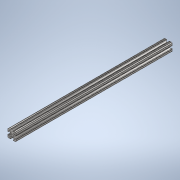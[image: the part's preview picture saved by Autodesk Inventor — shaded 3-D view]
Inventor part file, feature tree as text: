
AUTODESK INVENTOR PART (.ipt)
format: ipt  version: 2020 (Build 240168000, 168)  size: 241,152 bytes
history: native  units: in
note: dims shown in document units (in); Inventor stores cm internally (conversion verified against a paired STEP export)
features: extrude x1, sketch x1
ambient origin geometry x8: Origin, YZ Plane, XZ Plane, XY Plane, X Axis, Y Axis, Z Axis, Center Point
bodies: Solid1 (feature_tree)
feature tree (2):
  extrude  "Extrusion1"  [1 undecoded]
  sketch  "Sketch1"  dims[d0=19.0in d1=0.0in]
note: 1 required parameter value undecoded (feature->parameter linkage not recoverable at this tier; creation-order binding heuristic only, values carry confidence <= 0.55)
